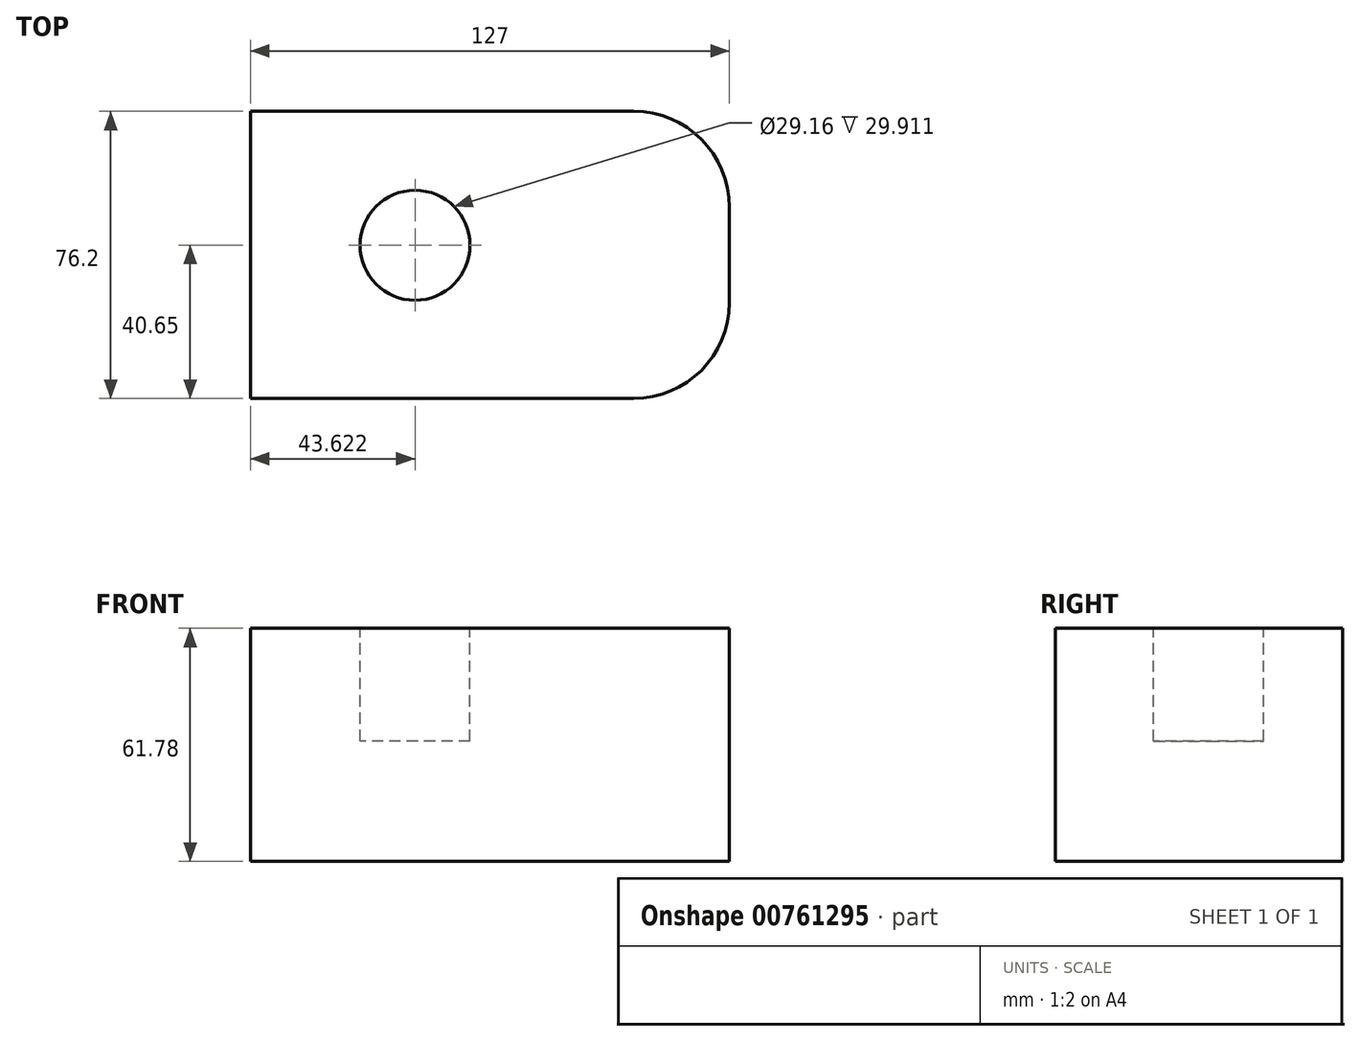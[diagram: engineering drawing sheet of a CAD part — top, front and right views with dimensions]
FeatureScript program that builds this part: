
annotation { "Feature Type Name" : "Feature", "Feature Type Description" : "" }
export const myFeature = defineFeature(function(context is Context, id is Id, definition is map)
    precondition{}
    {
        {
            var Q0;
            Q0=qCreatedBy(makeId("Top.planeOp"),FACE);
            var sketch = newSketch(context, id + "F0", { "sketchPlane" : qUnion([Q0])});
            skLineSegment(sketch, "E0.bottom", {"start": v(-65.92, 35.55) * mm, "end": v(61.08, 35.55) * mm});
            skLineSegment(sketch, "E0.top", {"start": v(-65.92, -40.65) * mm, "end": v(61.08, -40.65) * mm});
            skLineSegment(sketch, "E0.left", {"start": v(-65.92, 35.55) * mm, "end": v(-65.92, -40.65) * mm});
            skLineSegment(sketch, "E0.right", {"start": v(61.08, 35.55) * mm, "end": v(61.08, -40.65) * mm});
            skSolve(sketch);
        }
        {
            var Q0;
            Q0=makeQuery(id+"F0.imprint","IMPRINT",FACE,{"disambiguationData":[TD([[makeQuery(id+"F0.imprint","IMPRINT",EDGE,{"derivedFrom":sQuery(id+"F0.wireOp",EDGE,"E0.bottom")}),-1.0]])]});
            extrude(context, id + "F1", {"entities" : qUnion([Q0]), "depth" : 61.78 * mm, "offsetDistance" : 25.4 * mm});
        }
        {
            var Q0;
            Q0=makeQuery(id+"F1.opExtrude","SWEPT_EDGE",EDGE,{"disambiguationData":[OSD([sQuery(id+"F0.wireOp",EDGE,"E0.top"),sQuery(id+"F0.wireOp",EDGE,"E0.right")])]});
            var Q1;
            Q1=makeQuery(id+"F1.opExtrude","SWEPT_EDGE",EDGE,{"disambiguationData":[OSD([sQuery(id+"F0.wireOp",EDGE,"E0.bottom"),sQuery(id+"F0.wireOp",EDGE,"E0.right")])]});
            fillet(context, id + "F2", {"entities" : qUnion([Q0, Q1]), "radius" : 25.4 * mm, "tangentPropagation" : true, "allowEdgeOverflow" : false});
        }
        {
            var Q0;
            Q0=makeQuery(id+"F1.opExtrude","CAP_FACE",FACE,{"disambiguationData":[OSD([sQuery(id+"F0.wireOp",EDGE,"E0.bottom"),sQuery(id+"F0.wireOp",EDGE,"E0.top"),sQuery(id+"F0.wireOp",EDGE,"E0.left"),sQuery(id+"F0.wireOp",EDGE,"E0.right")])],"isStart":false});
            var sketch = newSketch(context, id + "F3", { "sketchPlane" : qUnion([Q0])});
            skCircle(sketch, "E1", {"center": v(-22.3, 0) * mm, "radius": 14.58 * mm});
            skSolve(sketch);
        }
        {
            var Q0;
            Q0=makeQuery(id+"F3.imprint","IMPRINT",FACE,{"disambiguationData":[TD([[makeQuery(id+"F3.imprint","IMPRINT",EDGE,{"derivedFrom":sQuery(id+"F3.wireOp",EDGE,"E1")}),1.0]])]});
            var Q1;
            Q1=sQuery(id+"F3.wireOp",EDGE,"E1");
            extrude(context, id + "F4", {"entities" : qUnion([Q0]), "operationType" : NewBodyOperationType.REMOVE, "surfaceEntities" : qUnion([Q1]), "oppositeDirection" : true, "depth" : 29.91 * mm, "offsetDistance" : 25.4 * mm});
        }
    });
